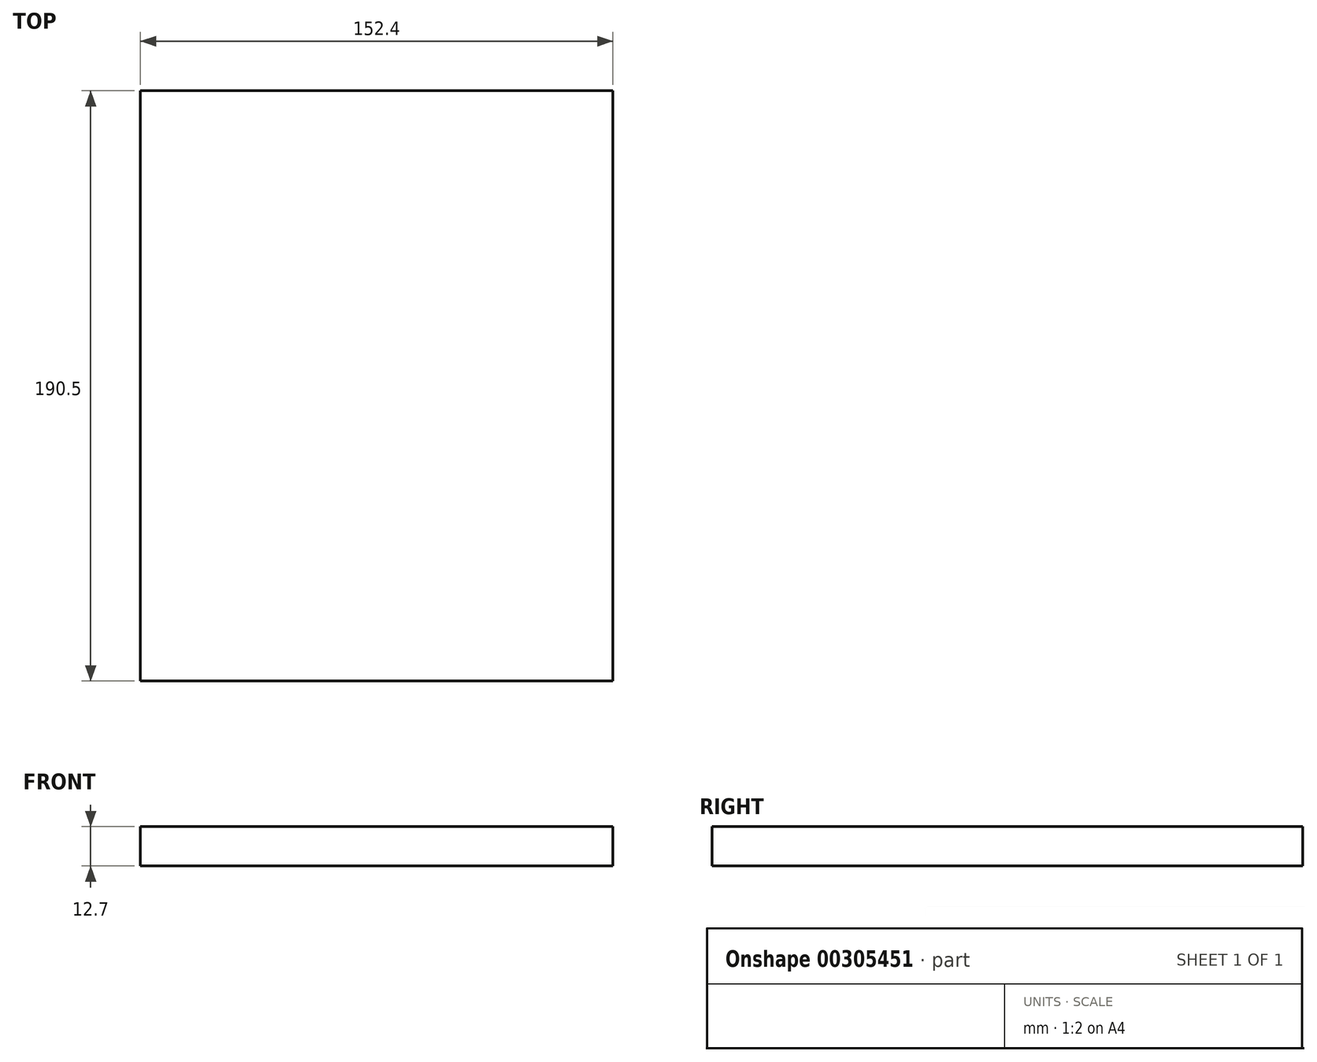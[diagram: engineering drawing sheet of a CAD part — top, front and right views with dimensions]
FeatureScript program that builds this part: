
annotation { "Feature Type Name" : "Feature", "Feature Type Description" : "" }
export const myFeature = defineFeature(function(context is Context, id is Id, definition is map)
    precondition{}
    {
        {
            var Q0;
            Q0=qCreatedBy(makeId("Top.planeOp"),FACE);
            var sketch = newSketch(context, id + "F0", { "sketchPlane" : qUnion([Q0])});
            skLineSegment(sketch, "E0.bottom", {"start": v(-57.09, -90.62) * mm, "end": v(95.31, -90.62) * mm});
            skLineSegment(sketch, "E0.top", {"start": v(-57.09, 99.88) * mm, "end": v(95.31, 99.88) * mm});
            skLineSegment(sketch, "E0.left", {"start": v(-57.09, -90.62) * mm, "end": v(-57.09, 99.88) * mm});
            skLineSegment(sketch, "E0.right", {"start": v(95.31, -90.62) * mm, "end": v(95.31, 99.88) * mm});
            skSolve(sketch);
        }
        {
            var Q0;
            Q0 = qSketchRegion(id + "F0", true);
            extrude(context, id + "F1", {"entities" : qUnion([Q0]), "depth" : 12.7 * mm});
        }
    });
